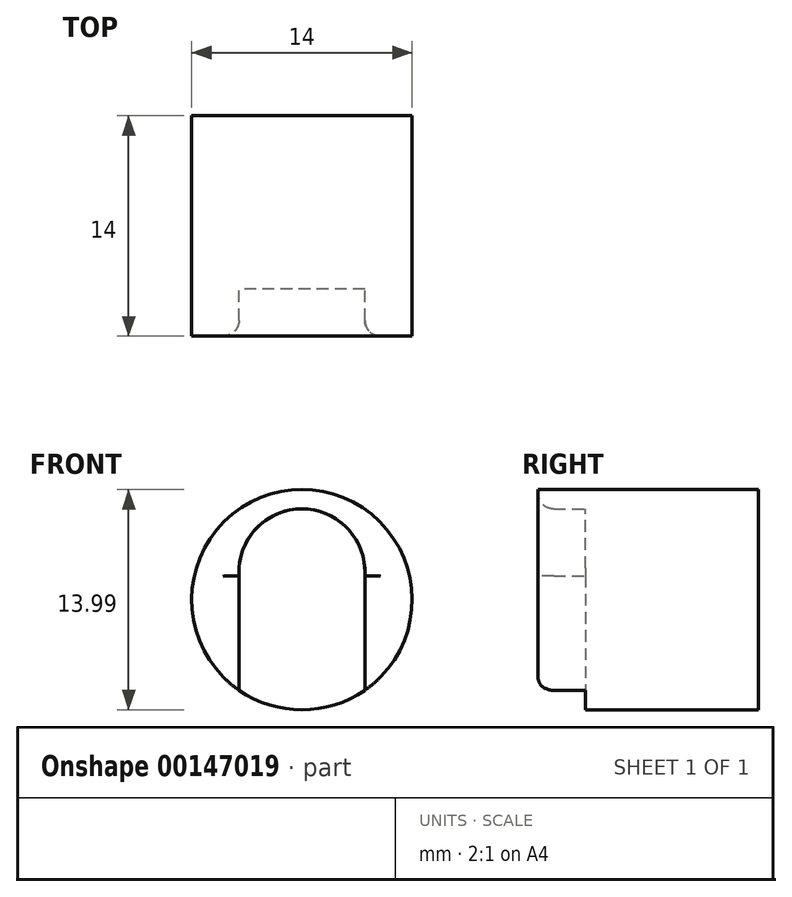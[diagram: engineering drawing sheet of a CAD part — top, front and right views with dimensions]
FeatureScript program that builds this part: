
annotation { "Feature Type Name" : "Feature", "Feature Type Description" : "" }
export const myFeature = defineFeature(function(context is Context, id is Id, definition is map)
    precondition{}
    {
        {
            var Q0;
            Q0=qCreatedBy(makeId("Front.planeOp"),FACE);
            var sketch = newSketch(context, id + "F0", { "sketchPlane" : qUnion([Q0])});
            skCircle(sketch, "E0", {"center": v(0, 0) * mm, "radius": 7 * mm});
            skCircle(sketch, "E1", {"center": v(0, 1.77) * mm, "radius": 4 * mm});
            skLineSegment(sketch, "E2", {"start": v(-4, 2.02) * mm, "end": v(-4, -5.75) * mm});
            skLineSegment(sketch, "E3", {"start": v(4, 2.02) * mm, "end": v(4, -5.75) * mm});
            skArc(sketch, "E4", {"start": v(-4, -5.75) * mm, "mid": v(0, -6.99) * mm, "end": v(4, -5.75) * mm});
            skSolve(sketch);
        }
        {
            var Q0;
            {var subQ1=sQuery(id+"F0.wireOp",EDGE,"E1");var subQ4=sQuery(id+"F0.wireOp",EDGE,"E2");var subQ5=makeQuery(id+"F0.imprint","INTERSECT",VERTEX,{"disambiguationData":[OD(0.0)],"derivedFrom":[subQ1,subQ4]});Q0=makeQuery(id+"F0.imprint","IMPRINT",FACE,{"disambiguationData":[TD([[makeQuery(id+"F0.imprint","IMPRINT",EDGE,{"disambiguationData":[TD([[subQ5,1.0]])],"derivedFrom":subQ1}),-1.0]])]});}
            extrude(context, id + "F1", {"entities" : qUnion([Q0]), "flatOperationType" : FlatOperationType.REMOVE, "depth" : 14 * mm, "offsetDistance" : 25 * mm, "domain" : OperationDomain.MODEL});
        }
        {
            var Q0;
            {var subQ5=sQuery(id+"F0.wireOp",EDGE,"E4");Q0=makeQuery(id+"F0.imprint","IMPRINT",FACE,{"disambiguationData":[TD([[makeQuery(id+"F0.imprint","IMPRINT",EDGE,{"derivedFrom":subQ5}),1.0]])]});}
            var Q1;
            {var subQ0=sQuery(id+"F0.wireOp",EDGE,"E2");var subQ1=sQuery(id+"F0.wireOp",EDGE,"E1");var subQ2=makeQuery(id+"F0.imprint","INTERSECT",VERTEX,{"disambiguationData":[OD(0.0)],"derivedFrom":[subQ1,subQ0]});Q1=makeQuery(id+"F0.imprint","IMPRINT",FACE,{"disambiguationData":[TD([[makeQuery(id+"F0.imprint","IMPRINT",EDGE,{"disambiguationData":[TD([[subQ2,1.0]])],"derivedFrom":subQ1}),1.0]])]});}
            extrude(context, id + "F2", {"entities" : qUnion([Q0, Q1]), "operationType" : NewBodyOperationType.ADD, "flatOperationType" : FlatOperationType.REMOVE, "depth" : 11 * mm, "offsetDistance" : 25 * mm, "domain" : OperationDomain.MODEL});
        }
        {
            var Q0;
            Q0=makeQuery(id+"F1.opExtrude","CAP_EDGE",EDGE,{"disambiguationData":[OSD([sQuery(id+"F0.wireOp",EDGE,"E1")])],"isStart":false});
            var Q1;
            Q1=makeQuery(id+"F1.opExtrude","CAP_EDGE",EDGE,{"disambiguationData":[OSD([sQuery(id+"F0.wireOp",EDGE,"E3")])],"isStart":false});
            var Q2;
            Q2=makeQuery(id+"F1.opExtrude","CAP_EDGE",EDGE,{"disambiguationData":[OSD([sQuery(id+"F0.wireOp",EDGE,"E2")])],"isStart":false});
            fillet(context, id + "F3", {"entities" : qUnion([Q0, Q1, Q2]), "radius" : 1 * mm, "tangentPropagation" : true, "allowEdgeOverflow" : false});
        }
    });
